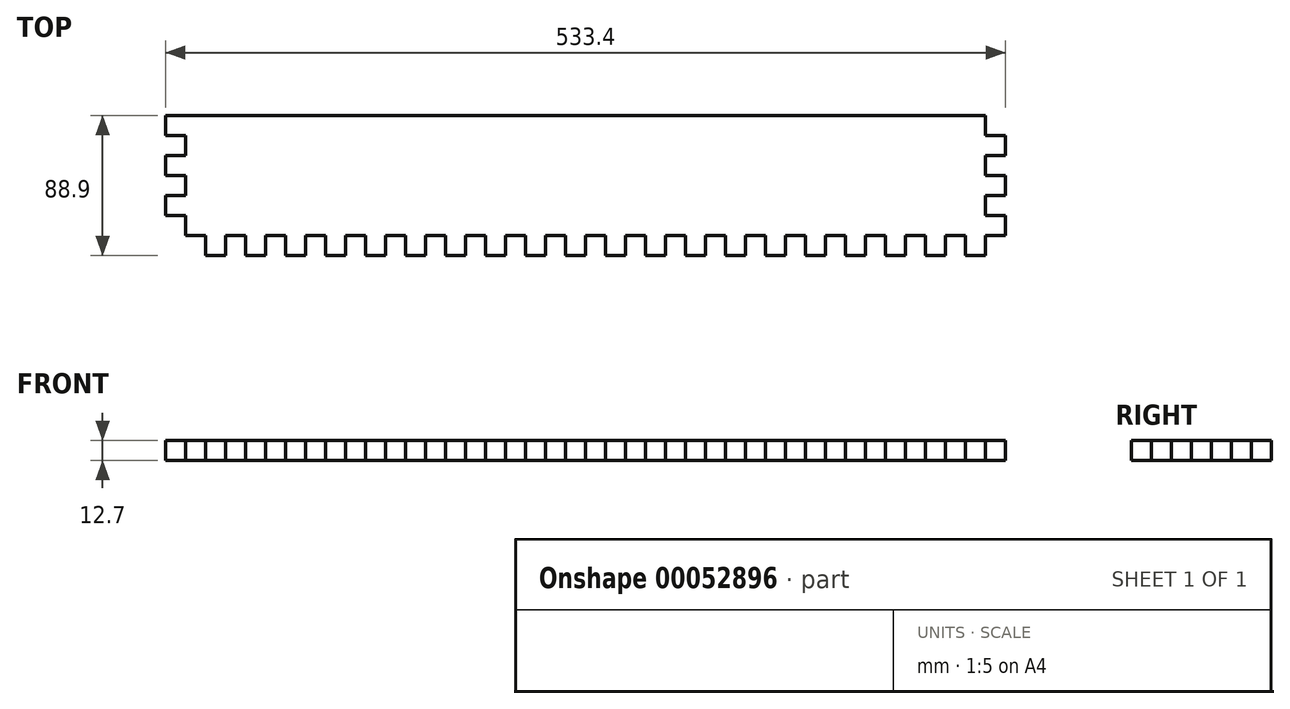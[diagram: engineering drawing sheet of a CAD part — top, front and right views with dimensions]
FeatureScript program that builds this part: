
annotation { "Feature Type Name" : "Feature", "Feature Type Description" : "" }
export const myFeature = defineFeature(function(context is Context, id is Id, definition is map)
    precondition{}
    {
        {
            var Q0;
            Q0=qCreatedBy(makeId("Top.planeOp"),FACE);
            var sketch = newSketch(context, id + "F0", { "sketchPlane" : qUnion([Q0])});
            skLineSegment(sketch, "E0.bottom", {"start": v(0, 0) * mm, "end": v(533.4, 0) * mm});
            skLineSegment(sketch, "E0.top", {"start": v(0, 88.9) * mm, "end": v(533.4, 88.9) * mm});
            skLineSegment(sketch, "E0.left", {"start": v(0, 0) * mm, "end": v(0, 88.9) * mm});
            skLineSegment(sketch, "E0.right", {"start": v(533.4, 0) * mm, "end": v(533.4, 88.9) * mm});
            skSolve(sketch);
        }
        {
            var Q0;
            Q0=qSketchRegion(id+"F0",true);
            extrude(context, id + "F1", {"entities" : qUnion([Q0]), "depth" : 12.7 * mm});
        }
        {
            var Q0;
            Q0=makeQuery(id+"F1.opExtrude","CAP_FACE",FACE,{"disambiguationData":[OSD([sQuery(id+"F0.wireOp",EDGE,"E0.bottom"),sQuery(id+"F0.wireOp",EDGE,"E0.top"),sQuery(id+"F0.wireOp",EDGE,"E0.left"),sQuery(id+"F0.wireOp",EDGE,"E0.right")])],"isStart":false});
            var sketch = newSketch(context, id + "F2", { "sketchPlane" : qUnion([Q0])});
            skLineSegment(sketch, "E1.bottom", {"start": v(533.4, 0) * mm, "end": v(520.7, 0) * mm});
            skLineSegment(sketch, "E1.top", {"start": v(533.4, 12.7) * mm, "end": v(520.7, 12.7) * mm});
            skLineSegment(sketch, "E1.left", {"start": v(533.4, 0) * mm, "end": v(533.4, 12.7) * mm});
            skLineSegment(sketch, "E1.right", {"start": v(520.7, 0) * mm, "end": v(520.7, 12.7) * mm});
            skLineSegment(sketch, "E2.bottom", {"start": v(533.4, 25.4) * mm, "end": v(520.7, 25.4) * mm});
            skLineSegment(sketch, "E2.top", {"start": v(533.4, 38.1) * mm, "end": v(520.7, 38.1) * mm});
            skLineSegment(sketch, "E2.left", {"start": v(533.4, 25.4) * mm, "end": v(533.4, 38.1) * mm});
            skLineSegment(sketch, "E2.right", {"start": v(520.7, 25.4) * mm, "end": v(520.7, 38.1) * mm});
            skLineSegment(sketch, "E3.bottom", {"start": v(533.4, 50.8) * mm, "end": v(520.7, 50.8) * mm});
            skLineSegment(sketch, "E3.top", {"start": v(533.4, 63.5) * mm, "end": v(520.7, 63.5) * mm});
            skLineSegment(sketch, "E3.left", {"start": v(533.4, 50.8) * mm, "end": v(533.4, 63.5) * mm});
            skLineSegment(sketch, "E3.right", {"start": v(520.7, 50.8) * mm, "end": v(520.7, 63.5) * mm});
            skLineSegment(sketch, "E4.bottom", {"start": v(533.4, 76.2) * mm, "end": v(520.7, 76.2) * mm});
            skLineSegment(sketch, "E4.top", {"start": v(533.4, 88.9) * mm, "end": v(520.7, 88.9) * mm});
            skLineSegment(sketch, "E4.left", {"start": v(533.4, 76.2) * mm, "end": v(533.4, 88.9) * mm});
            skLineSegment(sketch, "E4.right", {"start": v(520.7, 76.2) * mm, "end": v(520.7, 88.9) * mm});
            skSolve(sketch);
        }
        {
            var Q0;
            Q0=qSketchRegion(id+"F2",true);
            extrude(context, id + "F3", {"entities" : qUnion([Q0]), "operationType" : NewBodyOperationType.REMOVE, "oppositeDirection" : true, "depth" : 25.4 * mm});
        }
        {
            var Q0;
            Q0=makeQuery(id+"F1.opExtrude","CAP_FACE",FACE,{"disambiguationData":[OSD([sQuery(id+"F0.wireOp",EDGE,"E0.bottom"),sQuery(id+"F0.wireOp",EDGE,"E0.top"),sQuery(id+"F0.wireOp",EDGE,"E0.left"),sQuery(id+"F0.wireOp",EDGE,"E0.right")])],"isStart":false});
            var sketch = newSketch(context, id + "F4", { "sketchPlane" : qUnion([Q0])});
            skLineSegment(sketch, "E5.bottom", {"start": v(0, 38.1) * mm, "end": v(12.7, 38.1) * mm});
            skLineSegment(sketch, "E5.top", {"start": v(0, 50.8) * mm, "end": v(12.7, 50.8) * mm});
            skLineSegment(sketch, "E5.left", {"start": v(0, 38.1) * mm, "end": v(0, 50.8) * mm});
            skLineSegment(sketch, "E5.right", {"start": v(12.7, 38.1) * mm, "end": v(12.7, 50.8) * mm});
            skLineSegment(sketch, "E6.bottom", {"start": v(0, 63.5) * mm, "end": v(12.7, 63.5) * mm});
            skLineSegment(sketch, "E6.top", {"start": v(0, 76.2) * mm, "end": v(12.7, 76.2) * mm});
            skLineSegment(sketch, "E6.left", {"start": v(0, 63.5) * mm, "end": v(0, 76.2) * mm});
            skLineSegment(sketch, "E6.right", {"start": v(12.7, 63.5) * mm, "end": v(12.7, 76.2) * mm});
            skLineSegment(sketch, "E7.bottom", {"start": v(0, 0) * mm, "end": v(12.7, 0) * mm});
            skLineSegment(sketch, "E7.top", {"start": v(0, 25.4) * mm, "end": v(12.7, 25.4) * mm});
            skLineSegment(sketch, "E7.left", {"start": v(0, 0) * mm, "end": v(0, 25.4) * mm});
            skLineSegment(sketch, "E7.right", {"start": v(12.7, 0) * mm, "end": v(12.7, 25.4) * mm});
            skSolve(sketch);
        }
        {
            var Q0;
            Q0=qSketchRegion(id+"F4",true);
            extrude(context, id + "F5", {"entities" : qUnion([Q0]), "operationType" : NewBodyOperationType.REMOVE, "oppositeDirection" : true, "depth" : 25.4 * mm});
        }
        {
            var Q0;
            Q0=makeQuery(id+"F1.opExtrude","CAP_FACE",FACE,{"disambiguationData":[OSD([sQuery(id+"F0.wireOp",EDGE,"E0.bottom"),sQuery(id+"F0.wireOp",EDGE,"E0.top"),sQuery(id+"F0.wireOp",EDGE,"E0.left"),sQuery(id+"F0.wireOp",EDGE,"E0.right")])],"isStart":false});
            var sketch = newSketch(context, id + "F6", { "sketchPlane" : qUnion([Q0])});
            skLineSegment(sketch, "E8.bottom", {"start": v(12.7, 0) * mm, "end": v(25.4, 0) * mm});
            skLineSegment(sketch, "E8.top", {"start": v(12.7, 12.7) * mm, "end": v(25.4, 12.7) * mm});
            skLineSegment(sketch, "E8.left", {"start": v(12.7, 0) * mm, "end": v(12.7, 12.7) * mm});
            skLineSegment(sketch, "E8.right", {"start": v(25.4, 0) * mm, "end": v(25.4, 12.7) * mm});
            skLineSegment(sketch, "E9.bottom", {"start": v(38.1, 0) * mm, "end": v(50.8, 0) * mm});
            skLineSegment(sketch, "E9.top", {"start": v(38.1, 12.7) * mm, "end": v(50.8, 12.7) * mm});
            skLineSegment(sketch, "E9.left", {"start": v(38.1, 0) * mm, "end": v(38.1, 12.7) * mm});
            skLineSegment(sketch, "E9.right", {"start": v(50.8, 0) * mm, "end": v(50.8, 12.7) * mm});
            skLineSegment(sketch, "E10.bottom", {"start": v(63.5, 0) * mm, "end": v(76.2, 0) * mm});
            skLineSegment(sketch, "E10.top", {"start": v(63.5, 12.7) * mm, "end": v(76.2, 12.7) * mm});
            skLineSegment(sketch, "E10.left", {"start": v(63.5, 0) * mm, "end": v(63.5, 12.7) * mm});
            skLineSegment(sketch, "E10.right", {"start": v(76.2, 0) * mm, "end": v(76.2, 12.7) * mm});
            skLineSegment(sketch, "E11.bottom", {"start": v(88.9, 0) * mm, "end": v(101.6, 0) * mm});
            skLineSegment(sketch, "E11.top", {"start": v(88.9, 12.7) * mm, "end": v(101.6, 12.7) * mm});
            skLineSegment(sketch, "E11.left", {"start": v(88.9, 0) * mm, "end": v(88.9, 12.7) * mm});
            skLineSegment(sketch, "E11.right", {"start": v(101.6, 0) * mm, "end": v(101.6, 12.7) * mm});
            skLineSegment(sketch, "E12.bottom", {"start": v(114.3, 0) * mm, "end": v(127, 0) * mm});
            skLineSegment(sketch, "E12.top", {"start": v(114.3, 12.7) * mm, "end": v(127, 12.7) * mm});
            skLineSegment(sketch, "E12.left", {"start": v(114.3, 0) * mm, "end": v(114.3, 12.7) * mm});
            skLineSegment(sketch, "E12.right", {"start": v(127, 0) * mm, "end": v(127, 12.7) * mm});
            skLineSegment(sketch, "E13.bottom", {"start": v(139.7, 0) * mm, "end": v(152.4, 0) * mm});
            skLineSegment(sketch, "E13.top", {"start": v(139.7, 12.7) * mm, "end": v(152.4, 12.7) * mm});
            skLineSegment(sketch, "E13.left", {"start": v(139.7, 0) * mm, "end": v(139.7, 12.7) * mm});
            skLineSegment(sketch, "E13.right", {"start": v(152.4, 0) * mm, "end": v(152.4, 12.7) * mm});
            skLineSegment(sketch, "E14.bottom", {"start": v(165.1, 0) * mm, "end": v(177.8, 0) * mm});
            skLineSegment(sketch, "E14.top", {"start": v(165.1, 12.7) * mm, "end": v(177.8, 12.7) * mm});
            skLineSegment(sketch, "E14.left", {"start": v(165.1, 0) * mm, "end": v(165.1, 12.7) * mm});
            skLineSegment(sketch, "E14.right", {"start": v(177.8, 0) * mm, "end": v(177.8, 12.7) * mm});
            skLineSegment(sketch, "E15.bottom", {"start": v(190.5, 0) * mm, "end": v(203.2, 0) * mm});
            skLineSegment(sketch, "E15.top", {"start": v(190.5, 12.7) * mm, "end": v(203.2, 12.7) * mm});
            skLineSegment(sketch, "E15.left", {"start": v(190.5, 0) * mm, "end": v(190.5, 12.7) * mm});
            skLineSegment(sketch, "E15.right", {"start": v(203.2, 0) * mm, "end": v(203.2, 12.7) * mm});
            skLineSegment(sketch, "E16.bottom", {"start": v(215.9, 0) * mm, "end": v(228.6, 0) * mm});
            skLineSegment(sketch, "E16.top", {"start": v(215.9, 12.7) * mm, "end": v(228.6, 12.7) * mm});
            skLineSegment(sketch, "E16.left", {"start": v(215.9, 0) * mm, "end": v(215.9, 12.7) * mm});
            skLineSegment(sketch, "E16.right", {"start": v(228.6, 0) * mm, "end": v(228.6, 12.7) * mm});
            skLineSegment(sketch, "E17.bottom", {"start": v(241.3, 0) * mm, "end": v(254, 0) * mm});
            skLineSegment(sketch, "E17.top", {"start": v(241.3, 12.7) * mm, "end": v(254, 12.7) * mm});
            skLineSegment(sketch, "E17.left", {"start": v(241.3, 0) * mm, "end": v(241.3, 12.7) * mm});
            skLineSegment(sketch, "E17.right", {"start": v(254, 0) * mm, "end": v(254, 12.7) * mm});
            skLineSegment(sketch, "E18.bottom", {"start": v(266.7, 0) * mm, "end": v(279.4, 0) * mm});
            skLineSegment(sketch, "E18.top", {"start": v(266.7, 12.7) * mm, "end": v(279.4, 12.7) * mm});
            skLineSegment(sketch, "E18.left", {"start": v(266.7, 0) * mm, "end": v(266.7, 12.7) * mm});
            skLineSegment(sketch, "E18.right", {"start": v(279.4, 0) * mm, "end": v(279.4, 12.7) * mm});
            skLineSegment(sketch, "E19.bottom", {"start": v(292.1, 0) * mm, "end": v(304.8, 0) * mm});
            skLineSegment(sketch, "E19.top", {"start": v(292.1, 12.7) * mm, "end": v(304.8, 12.7) * mm});
            skLineSegment(sketch, "E19.left", {"start": v(292.1, 0) * mm, "end": v(292.1, 12.7) * mm});
            skLineSegment(sketch, "E19.right", {"start": v(304.8, 0) * mm, "end": v(304.8, 12.7) * mm});
            skLineSegment(sketch, "E20.bottom", {"start": v(317.5, 0) * mm, "end": v(330.2, 0) * mm});
            skLineSegment(sketch, "E20.top", {"start": v(317.5, 12.7) * mm, "end": v(330.2, 12.7) * mm});
            skLineSegment(sketch, "E20.left", {"start": v(317.5, 0) * mm, "end": v(317.5, 12.7) * mm});
            skLineSegment(sketch, "E20.right", {"start": v(330.2, 0) * mm, "end": v(330.2, 12.7) * mm});
            skLineSegment(sketch, "E21.bottom", {"start": v(355.6, 0) * mm, "end": v(342.9, 0) * mm});
            skLineSegment(sketch, "E21.top", {"start": v(355.6, 12.7) * mm, "end": v(342.9, 12.7) * mm});
            skLineSegment(sketch, "E21.left", {"start": v(355.6, 0) * mm, "end": v(355.6, 12.7) * mm});
            skLineSegment(sketch, "E21.right", {"start": v(342.9, 0) * mm, "end": v(342.9, 12.7) * mm});
            skLineSegment(sketch, "E22.bottom", {"start": v(368.3, 0) * mm, "end": v(381, 0) * mm});
            skLineSegment(sketch, "E22.top", {"start": v(368.3, 12.7) * mm, "end": v(381, 12.7) * mm});
            skLineSegment(sketch, "E22.left", {"start": v(368.3, 0) * mm, "end": v(368.3, 12.7) * mm});
            skLineSegment(sketch, "E22.right", {"start": v(381, 0) * mm, "end": v(381, 12.7) * mm});
            skLineSegment(sketch, "E23.bottom", {"start": v(393.7, 0) * mm, "end": v(406.4, 0) * mm});
            skLineSegment(sketch, "E23.top", {"start": v(393.7, 12.7) * mm, "end": v(406.4, 12.7) * mm});
            skLineSegment(sketch, "E23.left", {"start": v(393.7, 0) * mm, "end": v(393.7, 12.7) * mm});
            skLineSegment(sketch, "E23.right", {"start": v(406.4, 0) * mm, "end": v(406.4, 12.7) * mm});
            skLineSegment(sketch, "E24.bottom", {"start": v(419.1, 0) * mm, "end": v(431.8, 0) * mm});
            skLineSegment(sketch, "E24.top", {"start": v(419.1, 12.7) * mm, "end": v(431.8, 12.7) * mm});
            skLineSegment(sketch, "E24.left", {"start": v(419.1, 0) * mm, "end": v(419.1, 12.7) * mm});
            skLineSegment(sketch, "E24.right", {"start": v(431.8, 0) * mm, "end": v(431.8, 12.7) * mm});
            skLineSegment(sketch, "E25.bottom", {"start": v(444.5, 0) * mm, "end": v(457.2, 0) * mm});
            skLineSegment(sketch, "E25.top", {"start": v(444.5, 12.7) * mm, "end": v(457.2, 12.7) * mm});
            skLineSegment(sketch, "E25.left", {"start": v(444.5, 0) * mm, "end": v(444.5, 12.7) * mm});
            skLineSegment(sketch, "E25.right", {"start": v(457.2, 0) * mm, "end": v(457.2, 12.7) * mm});
            skLineSegment(sketch, "E26.bottom", {"start": v(469.9, 0) * mm, "end": v(482.6, 0) * mm});
            skLineSegment(sketch, "E26.top", {"start": v(469.9, 12.7) * mm, "end": v(482.6, 12.7) * mm});
            skLineSegment(sketch, "E26.left", {"start": v(469.9, 0) * mm, "end": v(469.9, 12.7) * mm});
            skLineSegment(sketch, "E26.right", {"start": v(482.6, 0) * mm, "end": v(482.6, 12.7) * mm});
            skLineSegment(sketch, "E27.bottom", {"start": v(495.3, 0) * mm, "end": v(508, 0) * mm});
            skLineSegment(sketch, "E27.top", {"start": v(495.3, 12.7) * mm, "end": v(508, 12.7) * mm});
            skLineSegment(sketch, "E27.left", {"start": v(495.3, 0) * mm, "end": v(495.3, 12.7) * mm});
            skLineSegment(sketch, "E27.right", {"start": v(508, 0) * mm, "end": v(508, 12.7) * mm});
            skSolve(sketch);
        }
        {
            var Q0;
            Q0 = qSketchRegion(id + "F6", true);
            extrude(context, id + "F7", {"entities" : qUnion([Q0]), "operationType" : NewBodyOperationType.REMOVE, "oppositeDirection" : true, "depth" : 25.4 * mm});
        }
    });
